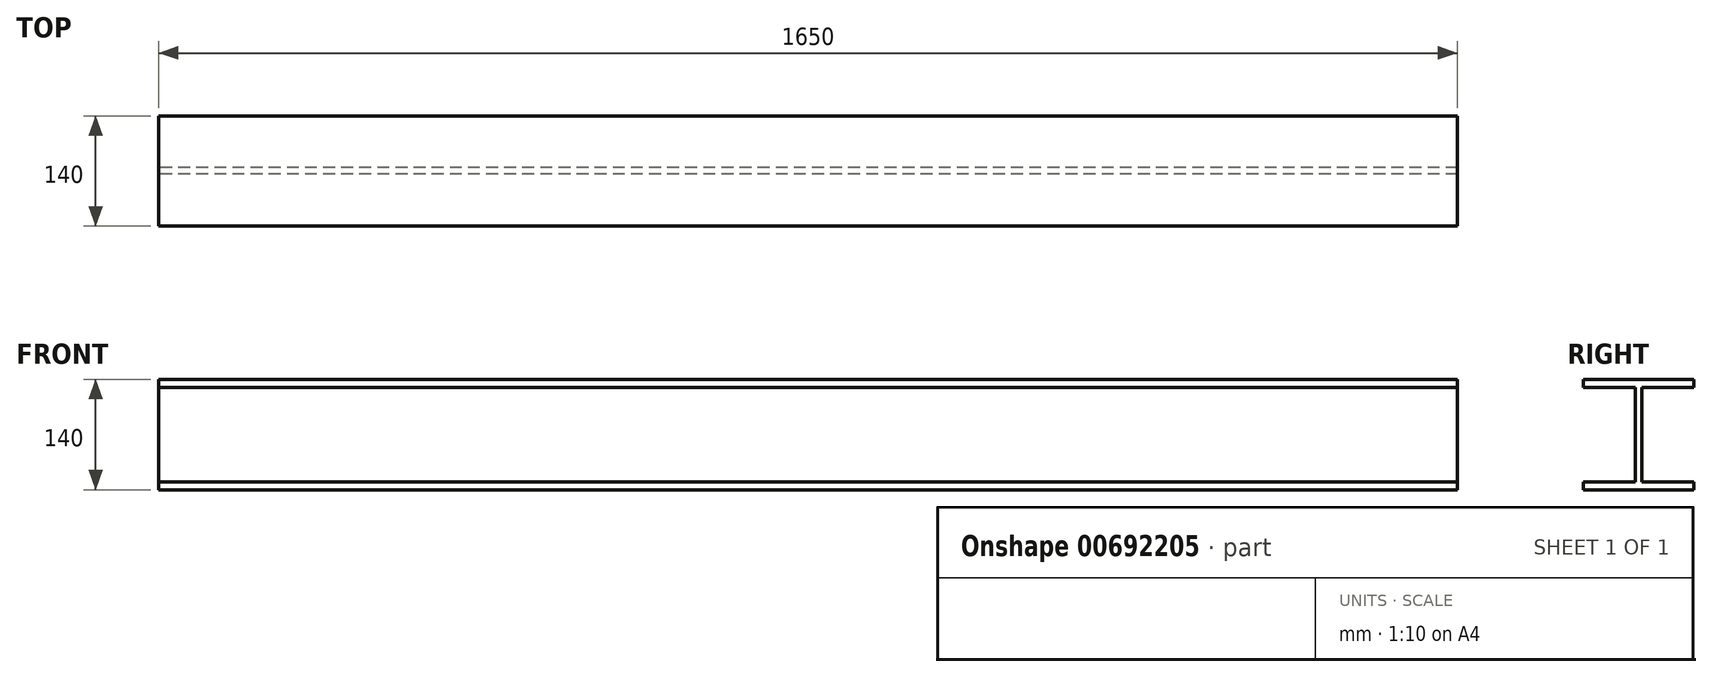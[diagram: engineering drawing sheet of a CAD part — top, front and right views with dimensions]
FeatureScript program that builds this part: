
annotation { "Feature Type Name" : "Feature", "Feature Type Description" : "" }
export const myFeature = defineFeature(function(context is Context, id is Id, definition is map)
    precondition{}
    {
        {
            var Q0;
            Q0=qCreatedBy(makeId("Right.planeOp"),FACE);
            var sketch = newSketch(context, id + "F0", { "sketchPlane" : qUnion([Q0])});
            skLineSegment(sketch, "E0", {"start": v(70, 70) * mm, "end": v(-70, 70) * mm});
            skLineSegment(sketch, "E1", {"start": v(-70, 70) * mm, "end": v(-70, 60) * mm});
            skLineSegment(sketch, "E2", {"start": v(-70, 60) * mm, "end": v(-4, 60) * mm});
            skLineSegment(sketch, "E3", {"start": v(-4, 60) * mm, "end": v(-4, -60) * mm});
            skLineSegment(sketch, "E4", {"start": v(-4, -60) * mm, "end": v(-70, -60) * mm});
            skLineSegment(sketch, "E5", {"start": v(-70, -60) * mm, "end": v(-70, -70) * mm});
            skLineSegment(sketch, "E6", {"start": v(-70, -70) * mm, "end": v(70, -70) * mm});
            skLineSegment(sketch, "E7", {"start": v(70, -70) * mm, "end": v(70, -60) * mm});
            skLineSegment(sketch, "E8", {"start": v(70, -60) * mm, "end": v(4, -60) * mm});
            skLineSegment(sketch, "E9", {"start": v(4, -60) * mm, "end": v(4, 60) * mm});
            skLineSegment(sketch, "E10", {"start": v(4, 60) * mm, "end": v(70, 60) * mm});
            skLineSegment(sketch, "E11", {"start": v(70, 60) * mm, "end": v(70, 70) * mm});
            skSolve(sketch);
        }
        {
            var Q0;
            Q0=makeQuery(id+"F0.imprint","IMPRINT",FACE,{"disambiguationData":[TD([[makeQuery(id+"F0.imprint","IMPRINT",EDGE,{"derivedFrom":sQuery(id+"F0.wireOp",EDGE,"E0")}),1.0]])]});
            extrude(context, id + "F1", {"entities" : qUnion([Q0]), "endBound" : BoundingType.SYMMETRIC, "depth" : 1650 * mm, "offsetDistance" : 25 * mm});
        }
    });
